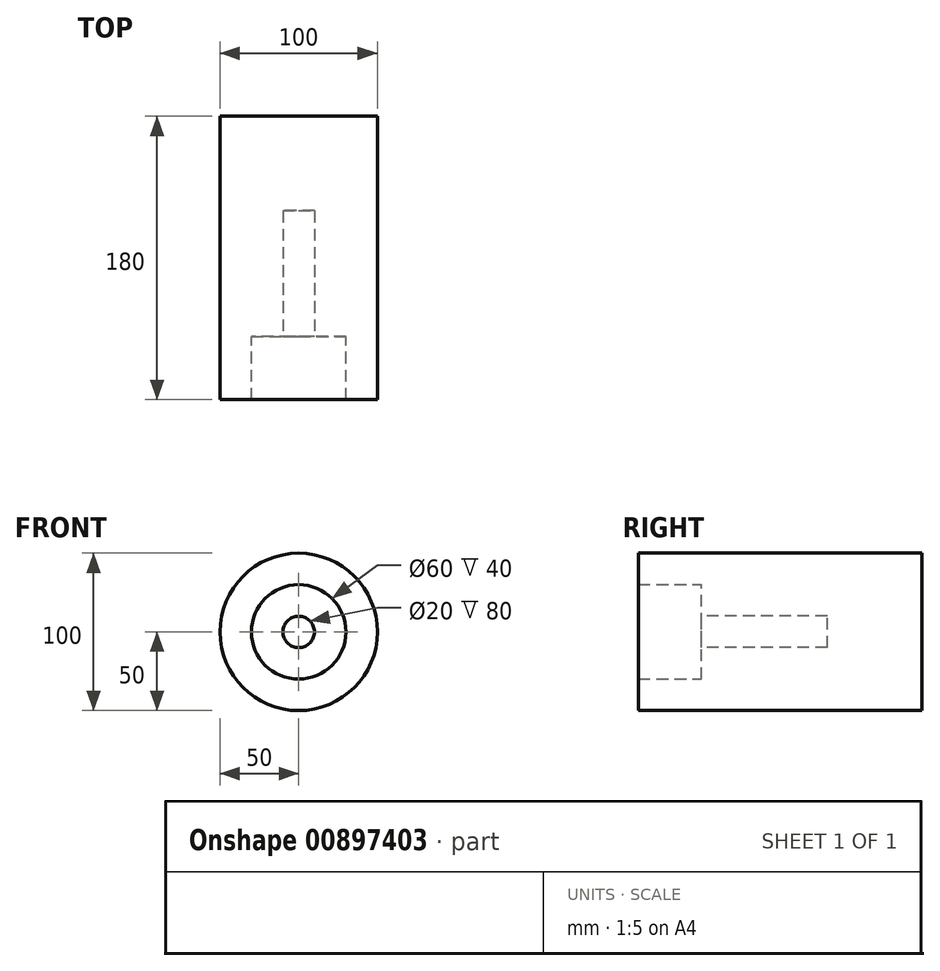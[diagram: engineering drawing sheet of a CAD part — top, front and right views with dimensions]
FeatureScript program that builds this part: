
annotation { "Feature Type Name" : "Feature", "Feature Type Description" : "" }
export const myFeature = defineFeature(function(context is Context, id is Id, definition is map)
    precondition{}
    {
        {
            var Q0;
            Q0=qCreatedBy(makeId("Front.planeOp"),FACE);
            var sketch = newSketch(context, id + "F0", { "sketchPlane" : qUnion([Q0])});
            skCircle(sketch, "E0", {"center": v(0, 0) * mm, "radius": 50 * mm});
            skSolve(sketch);
        }
        {
            var Q0;
            Q0 = qSketchRegion(id + "F0", true);
            var Q1;
            Q1=makeQuery(id+"F0.imprint","IMPRINT",FACE,{"disambiguationData":[TD([[makeQuery(id+"F0.imprint","IMPRINT",EDGE,{"derivedFrom":sQuery(id+"F0.wireOp",EDGE,"E0")}),1.0]])]});
            extrude(context, id + "F1", {"entities" : qUnion([Q0, Q1]), "depth" : 140 * mm, "offsetDistance" : 25.4 * mm});
        }
        {
            var Q0;
            Q0=makeQuery(id+"F1.opExtrude","CAP_FACE",FACE,{"disambiguationData":[OSD([sQuery(id+"F0.wireOp",EDGE,"E0")])],"isStart":false});
            var sketch = newSketch(context, id + "F2", { "sketchPlane" : qUnion([Q0])});
            skCircle(sketch, "E1", {"center": v(0, 0) * mm, "radius": 30 * mm});
            skSolve(sketch);
        }
        {
            var Q0;
            Q0=makeQuery(id+"F2.imprint","IMPRINT",FACE,{"disambiguationData":[TD([[makeQuery(id+"F2.imprint","IMPRINT",EDGE,{"derivedFrom":sQuery(id+"F2.wireOp",EDGE,"E1")}),-1.0]])]});
            extrude(context, id + "F3", {"entities" : qUnion([Q0]), "operationType" : NewBodyOperationType.ADD, "depth" : 40 * mm, "offsetDistance" : 25.4 * mm});
        }
        {
            var Q0;
            Q0=makeQuery(id+"F1.opExtrude","CAP_FACE",FACE,{"disambiguationData":[OSD([sQuery(id+"F0.wireOp",EDGE,"E0")])],"isStart":false});
            var sketch = newSketch(context, id + "F4", { "sketchPlane" : qUnion([Q0])});
            skCircle(sketch, "E2", {"center": v(0, 0) * mm, "radius": 10 * mm});
            skSolve(sketch);
        }
        {
            var Q0;
            Q0=makeQuery(id+"F4.imprint","IMPRINT",FACE,{"disambiguationData":[TD([[makeQuery(id+"F4.imprint","IMPRINT",EDGE,{"derivedFrom":sQuery(id+"F4.wireOp",EDGE,"E2")}),1.0]])]});
            extrude(context, id + "F5", {"entities" : qUnion([Q0]), "operationType" : NewBodyOperationType.REMOVE, "oppositeDirection" : true, "depth" : 80 * mm, "offsetDistance" : 25.4 * mm});
        }
    });
